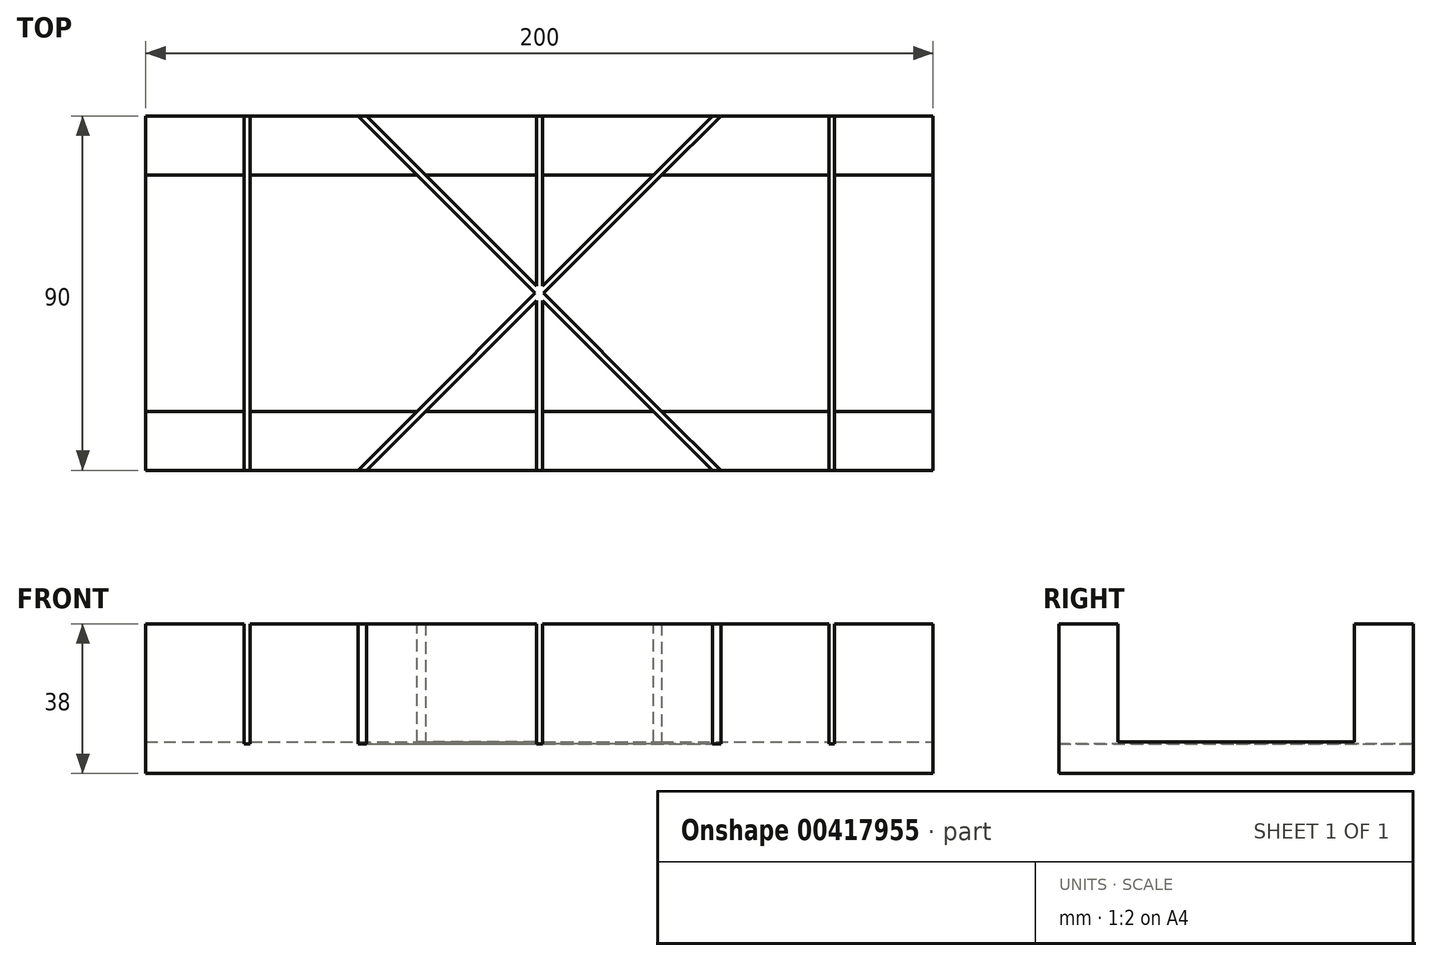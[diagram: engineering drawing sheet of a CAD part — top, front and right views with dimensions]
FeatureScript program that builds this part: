
annotation { "Feature Type Name" : "Feature", "Feature Type Description" : "" }
export const myFeature = defineFeature(function(context is Context, id is Id, definition is map)
    precondition{}
    {
        {
            var Q0;
            Q0=qCreatedBy(makeId("Top.planeOp"),FACE);
            var sketch = newSketch(context, id + "F0", { "sketchPlane" : qUnion([Q0])});
            skLineSegment(sketch, "E0.bottom", {"start": v(-100, -45) * mm, "end": v(100, -45) * mm});
            skLineSegment(sketch, "E0.top", {"start": v(-100, 45) * mm, "end": v(100, 45) * mm});
            skLineSegment(sketch, "E0.left", {"start": v(-100, -45) * mm, "end": v(-100, 45) * mm});
            skLineSegment(sketch, "E0.right", {"start": v(100, -45) * mm, "end": v(100, 45) * mm});
            skSolve(sketch);
        }
        {
            var Q0;
            Q0 = qSketchRegion(id + "F0", true);
            extrude(context, id + "F1", {"entities" : qUnion([Q0]), "depth" : 8 * mm});
        }
        {
            var Q0;
            Q0=makeQuery(id+"F1.opExtrude","CAP_FACE",FACE,{"disambiguationData":[OSD([sQuery(id+"F0.wireOp",EDGE,"E0.bottom"),sQuery(id+"F0.wireOp",EDGE,"E0.top"),sQuery(id+"F0.wireOp",EDGE,"E0.left"),sQuery(id+"F0.wireOp",EDGE,"E0.right")])],"isStart":false});
            var sketch = newSketch(context, id + "F2", { "sketchPlane" : qUnion([Q0])});
            skLineSegment(sketch, "E1.bottom", {"start": v(-100, 45) * mm, "end": v(100, 45) * mm});
            skLineSegment(sketch, "E1.top", {"start": v(-100, 30) * mm, "end": v(100, 30) * mm});
            skLineSegment(sketch, "E1.left", {"start": v(-100, 45) * mm, "end": v(-100, 30) * mm});
            skLineSegment(sketch, "E1.right", {"start": v(100, 45) * mm, "end": v(100, 30) * mm});
            skLineSegment(sketch, "E2.bottom", {"start": v(100, -45) * mm, "end": v(-100, -45) * mm});
            skLineSegment(sketch, "E2.top", {"start": v(100, -30) * mm, "end": v(-100, -30) * mm});
            skLineSegment(sketch, "E2.left", {"start": v(100, -45) * mm, "end": v(100, -30) * mm});
            skLineSegment(sketch, "E2.right", {"start": v(-100, -45) * mm, "end": v(-100, -30) * mm});
            skSolve(sketch);
        }
        {
            var Q0;
            Q0 = qSketchRegion(id + "F2", true);
            extrude(context, id + "F3", {"entities" : qUnion([Q0]), "operationType" : NewBodyOperationType.ADD, "depth" : 30 * mm});
        }
        {
            var Q0;
            Q0=makeQuery(id+"F3.opExtrude","CAP_FACE",FACE,{"disambiguationData":[OSD([sQuery(id+"F2.wireOp",EDGE,"E2.bottom"),sQuery(id+"F2.wireOp",EDGE,"E2.top"),sQuery(id+"F2.wireOp",EDGE,"E2.left"),sQuery(id+"F2.wireOp",EDGE,"E2.right")])],"isStart":false});
            var sketch = newSketch(context, id + "F4", { "sketchPlane" : qUnion([Q0])});
            skLineSegment(sketch, "E3.bottom", {"start": v(-0.75, 60) * mm, "end": v(0.75, 60) * mm});
            skLineSegment(sketch, "E3.top", {"start": v(-0.75, -70) * mm, "end": v(0.75, -70) * mm});
            skLineSegment(sketch, "E3.left", {"start": v(-0.75, 60) * mm, "end": v(-0.75, 1.81) * mm});
            skLineSegment(sketch, "E3.right", {"start": v(0.75, 60) * mm, "end": v(0.75, 1.81) * mm});
            skLineSegment(sketch, "E4.bottom", {"start": v(-75, 59.26) * mm, "end": v(-73.5, 59.26) * mm});
            skLineSegment(sketch, "E4.top", {"start": v(-75, -66.86) * mm, "end": v(-73.5, -66.86) * mm});
            skLineSegment(sketch, "E4.left", {"start": v(-75, 59.26) * mm, "end": v(-75, -66.86) * mm});
            skLineSegment(sketch, "E4.right", {"start": v(-73.5, 59.26) * mm, "end": v(-73.5, -66.86) * mm});
            skLineSegment(sketch, "E5.bottom", {"start": v(73.5, 59.7) * mm, "end": v(75, 59.7) * mm});
            skLineSegment(sketch, "E5.top", {"start": v(73.5, -72.94) * mm, "end": v(75, -72.94) * mm});
            skLineSegment(sketch, "E5.left", {"start": v(73.5, 59.7) * mm, "end": v(73.5, -72.94) * mm});
            skLineSegment(sketch, "E5.right", {"start": v(75, 59.7) * mm, "end": v(75, -72.94) * mm});
            skLineSegment(sketch, "E6", {"start": v(-46.07, -47.13) * mm, "end": v(0, -1.06) * mm});
            skLineSegment(sketch, "E7", {"start": v(58.94, 60) * mm, "end": v(60, 58.94) * mm});
            skLineSegment(sketch, "E8", {"start": v(58.94, 60) * mm, "end": v(0, 1.06) * mm});
            skLineSegment(sketch, "E9", {"start": v(-47.13, -46.07) * mm, "end": v(-46.07, -47.13) * mm});
            skLineSegment(sketch, "E10", {"start": v(-47.13, 48.19) * mm, "end": v(-48.19, 47.13) * mm});
            skLineSegment(sketch, "E11", {"start": v(-48.19, 47.13) * mm, "end": v(-1.06, 0) * mm});
            skLineSegment(sketch, "E12", {"start": v(57.88, -58.94) * mm, "end": v(58.94, -57.88) * mm});
            skLineSegment(sketch, "E13", {"start": v(58.94, -57.88) * mm, "end": v(1.06, 0) * mm});
            skLineSegment(sketch, "E14.trimOffspring", {"start": v(-0.75, -1.81) * mm, "end": v(-0.75, -70) * mm});
            skLineSegment(sketch, "E15.trimOffspring", {"start": v(0, -1.06) * mm, "end": v(57.88, -58.94) * mm});
            skLineSegment(sketch, "E16.trimOffspring", {"start": v(-1.06, 0) * mm, "end": v(-47.13, -46.07) * mm});
            skLineSegment(sketch, "E17.trimOffspring", {"start": v(0, 1.06) * mm, "end": v(-47.13, 48.19) * mm});
            skLineSegment(sketch, "E18.trimOffspring", {"start": v(0.75, -1.81) * mm, "end": v(0.75, -70) * mm});
            skLineSegment(sketch, "E19.trimOffspring", {"start": v(1.06, 0) * mm, "end": v(60, 58.94) * mm});
            skSolve(sketch);
        }
        {
            var Q0;
            Q0 = qSketchRegion(id + "F4", true);
            extrude(context, id + "F5", {"entities" : qUnion([Q0]), "operationType" : NewBodyOperationType.REMOVE, "oppositeDirection" : true, "depth" : 30.5 * mm});
        }
    });
